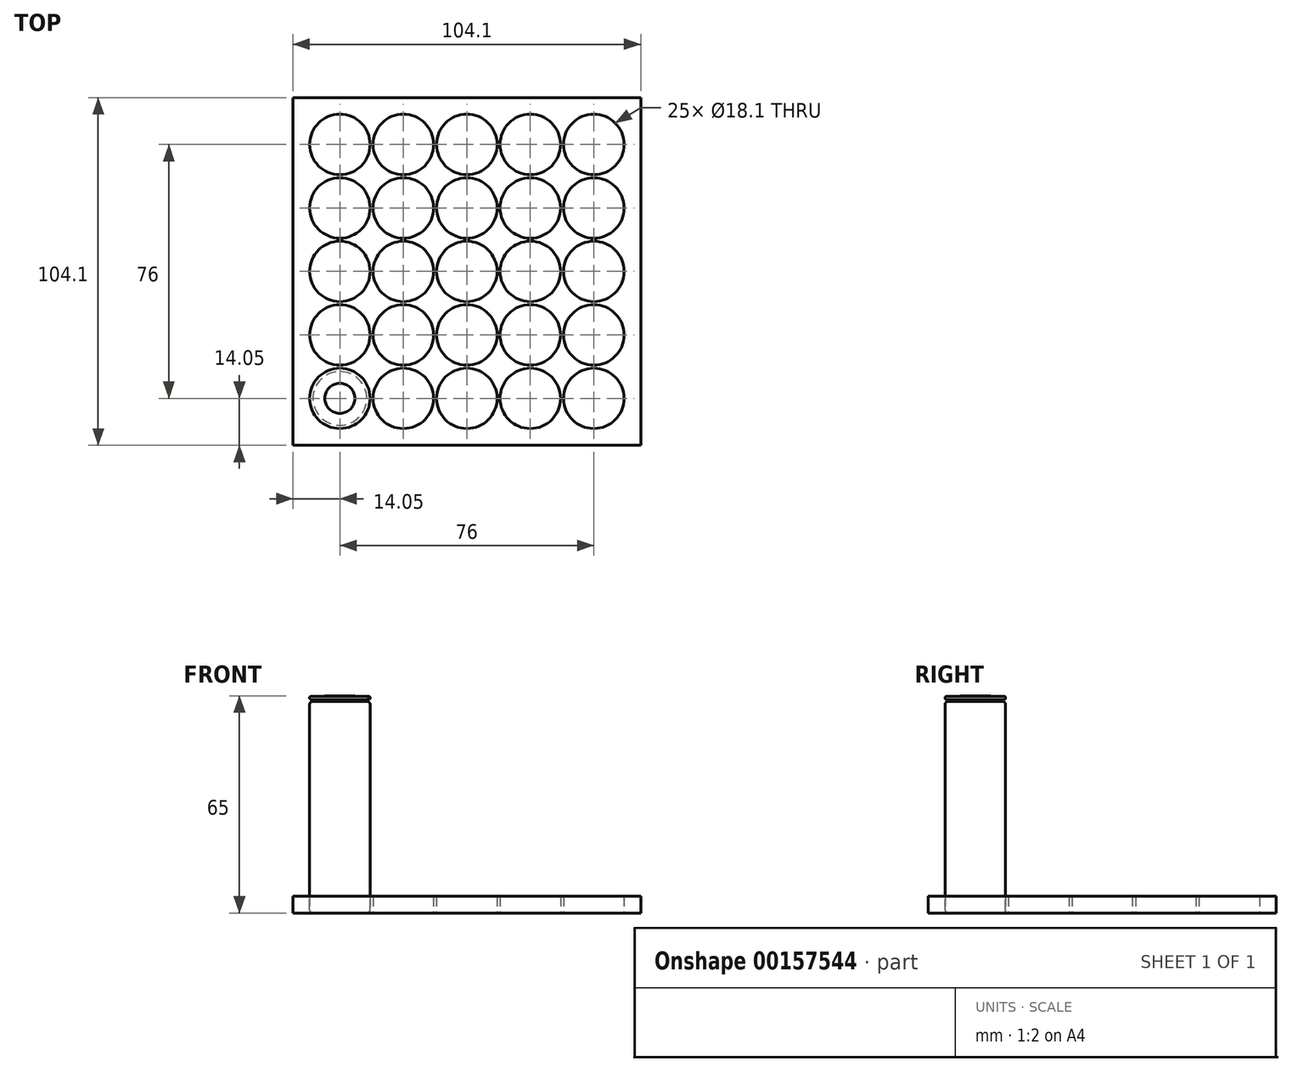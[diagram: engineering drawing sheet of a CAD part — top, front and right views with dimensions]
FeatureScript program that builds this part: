
annotation { "Feature Type Name" : "Feature", "Feature Type Description" : "" }
export const myFeature = defineFeature(function(context is Context, id is Id, definition is map)
    precondition{}
    {
        {
            var Q0;
            Q0=qCreatedBy(makeId("Front.planeOp"),FACE);
            var sketch = newSketch(context, id + "F0", { "sketchPlane" : qUnion([Q0])});
            skLineSegment(sketch, "E0.bottom", {"start": v(0, 0) * mm, "end": v(9.05, 0) * mm});
            skLineSegment(sketch, "E0.top", {"start": v(4.5, 64.8) * mm, "end": v(9.05, 64.8) * mm});
            skLineSegment(sketch, "E0.right", {"start": v(9.05, 0) * mm, "end": v(9.05, 63.37) * mm});
            skLineSegment(sketch, "E1.top", {"start": v(0, 65) * mm, "end": v(4.5, 65) * mm});
            skLineSegment(sketch, "E1.right", {"start": v(4.5, 64.8) * mm, "end": v(4.5, 65) * mm});
            skLineSegment(sketch, "E2", {"start": v(0, 65) * mm, "end": v(0, 0) * mm});
            skLineSegment(sketch, "E3", {"start": v(8.05, 63.87) * mm, "end": v(8.05, 63.37) * mm});
            skLineSegment(sketch, "E4", {"start": v(8.05, 63.37) * mm, "end": v(9.05, 63.37) * mm});
            skLineSegment(sketch, "E5.trimOffspring", {"start": v(9.05, 64.05) * mm, "end": v(9.05, 64.8) * mm});
            skLineSegment(sketch, "E6", {"start": v(8.05, 63.87) * mm, "end": v(9.05, 64.05) * mm});
            skSolve(sketch);
        }
        {
            var Q0;
            Q0 = qSketchRegion(id + "F0", true);
            var Q1;
            Q1=sQuery(id+"F0.wireOp",EDGE,"E2");
            revolve(context, id + "F1", {"entities" : qUnion([Q0]), "axis" : qUnion([Q1]), "revolveType" : RevolveType.FULL});
        }
        {
            var Q0;
            Q0=makeQuery(id+"F1.opRevolve","SWEPT_EDGE",EDGE,{"disambiguationData":[OSD([sQuery(id+"F0.wireOp",EDGE,"E0.bottom"),sQuery(id+"F0.wireOp",EDGE,"E0.right")])]});
            var Q1;
            Q1=makeQuery(id+"F1.opRevolve","SWEPT_EDGE",EDGE,{"disambiguationData":[OSD([sQuery(id+"F0.wireOp",EDGE,"E0.right"),sQuery(id+"F0.wireOp",EDGE,"E4")])]});
            fillet(context, id + "F2", {"entities" : qUnion([Q0, Q1]), "radius" : 1 * mm, "tangentPropagation" : true, "allowEdgeOverflow" : false});
        }
        {
            var Q0;
            Q0=makeQuery(id+"F1.opRevolve","SWEPT_EDGE",EDGE,{"disambiguationData":[OSD([sQuery(id+"F0.wireOp",EDGE,"E5.trimOffspring"),sQuery(id+"F0.wireOp",EDGE,"E6")])]});
            var Q1;
            Q1=makeQuery(id+"F1.opRevolve","SWEPT_EDGE",EDGE,{"disambiguationData":[OSD([sQuery(id+"F0.wireOp",EDGE,"E0.top"),sQuery(id+"F0.wireOp",EDGE,"E5.trimOffspring")])]});
            fillet(context, id + "F3", {"entities" : qUnion([Q0, Q1]), "radius" : 0.3 * mm, "tangentPropagation" : true, "allowEdgeOverflow" : false});
        }
        {
            var Q0;
            Q0=qCreatedBy(makeId("Top.planeOp"),FACE);
            var sketch = newSketch(context, id + "F4", { "sketchPlane" : qUnion([Q0])});
            skCircle(sketch, "E7", {"center": v(0, 0) * mm, "radius": 9.05 * mm});
            skCircle(sketch, "E8.0.1.0", {"center": v(0, 19) * mm, "radius": 9.05 * mm});
            skCircle(sketch, "E8.0.2.0", {"center": v(0, 38) * mm, "radius": 9.05 * mm});
            skCircle(sketch, "E8.0.3.0", {"center": v(0, 57) * mm, "radius": 9.05 * mm});
            skCircle(sketch, "E8.1.0.0", {"center": v(19, 0) * mm, "radius": 9.05 * mm});
            skCircle(sketch, "E8.1.1.0", {"center": v(19, 19) * mm, "radius": 9.05 * mm});
            skCircle(sketch, "E8.1.2.0", {"center": v(19, 38) * mm, "radius": 9.05 * mm});
            skCircle(sketch, "E8.1.3.0", {"center": v(19, 57) * mm, "radius": 9.05 * mm});
            skLineSegment(sketch, "E8.direction1", {"start": v(0, 0) * mm, "end": v(19, 0) * mm, "construction": true});
            skLineSegment(sketch, "E8.direction2", {"start": v(0, 0) * mm, "end": v(0, 19) * mm, "construction": true});
            skLineSegment(sketch, "E9.bottom", {"start": v(-14.05, 90.05) * mm, "end": v(90.05, 90.05) * mm});
            skLineSegment(sketch, "E9.top", {"start": v(-14.05, -14.05) * mm, "end": v(90.05, -14.05) * mm});
            skLineSegment(sketch, "E9.left", {"start": v(-14.05, 90.05) * mm, "end": v(-14.05, -14.05) * mm});
            skLineSegment(sketch, "E9.right", {"start": v(90.05, 90.05) * mm, "end": v(90.05, -14.05) * mm});
            skCircle(sketch, "E10.0.0.4", {"center": v(0, 76) * mm, "radius": 9.05 * mm});
            skCircle(sketch, "E10.0.1.4", {"center": v(19, 76) * mm, "radius": 9.05 * mm});
            skCircle(sketch, "E11.0.2.0", {"center": v(38, 0) * mm, "radius": 9.05 * mm});
            skCircle(sketch, "E11.0.2.1", {"center": v(38, 19) * mm, "radius": 9.05 * mm});
            skCircle(sketch, "E11.0.2.2", {"center": v(38, 38) * mm, "radius": 9.05 * mm});
            skCircle(sketch, "E11.0.2.3", {"center": v(38, 57) * mm, "radius": 9.05 * mm});
            skCircle(sketch, "E11.0.2.4", {"center": v(38, 76) * mm, "radius": 9.05 * mm});
            skCircle(sketch, "E11.0.3.0", {"center": v(57, 0) * mm, "radius": 9.05 * mm});
            skCircle(sketch, "E11.0.3.1", {"center": v(57, 19) * mm, "radius": 9.05 * mm});
            skCircle(sketch, "E11.0.3.2", {"center": v(57, 38) * mm, "radius": 9.05 * mm});
            skCircle(sketch, "E11.0.3.3", {"center": v(57, 57) * mm, "radius": 9.05 * mm});
            skCircle(sketch, "E11.0.3.4", {"center": v(57, 76) * mm, "radius": 9.05 * mm});
            skCircle(sketch, "E12.0.4.0", {"center": v(76, 0) * mm, "radius": 9.05 * mm});
            skCircle(sketch, "E12.0.4.1", {"center": v(76, 19) * mm, "radius": 9.05 * mm});
            skCircle(sketch, "E12.0.4.2", {"center": v(76, 38) * mm, "radius": 9.05 * mm});
            skCircle(sketch, "E12.0.4.3", {"center": v(76, 57) * mm, "radius": 9.05 * mm});
            skCircle(sketch, "E12.0.4.4", {"center": v(76, 76) * mm, "radius": 9.05 * mm});
            skSolve(sketch);
        }
        {
            var Q0;
            Q0=makeQuery(id+"F4.imprint","IMPRINT",FACE,{"disambiguationData":[TD([[makeQuery(id+"F4.imprint","IMPRINT",EDGE,{"derivedFrom":sQuery(id+"F4.wireOp",EDGE,"E7")}),-1.0]])]});
            extrude(context, id + "F5", {"entities" : qUnion([Q0]), "depth" : 5 * mm});
        }
    });
